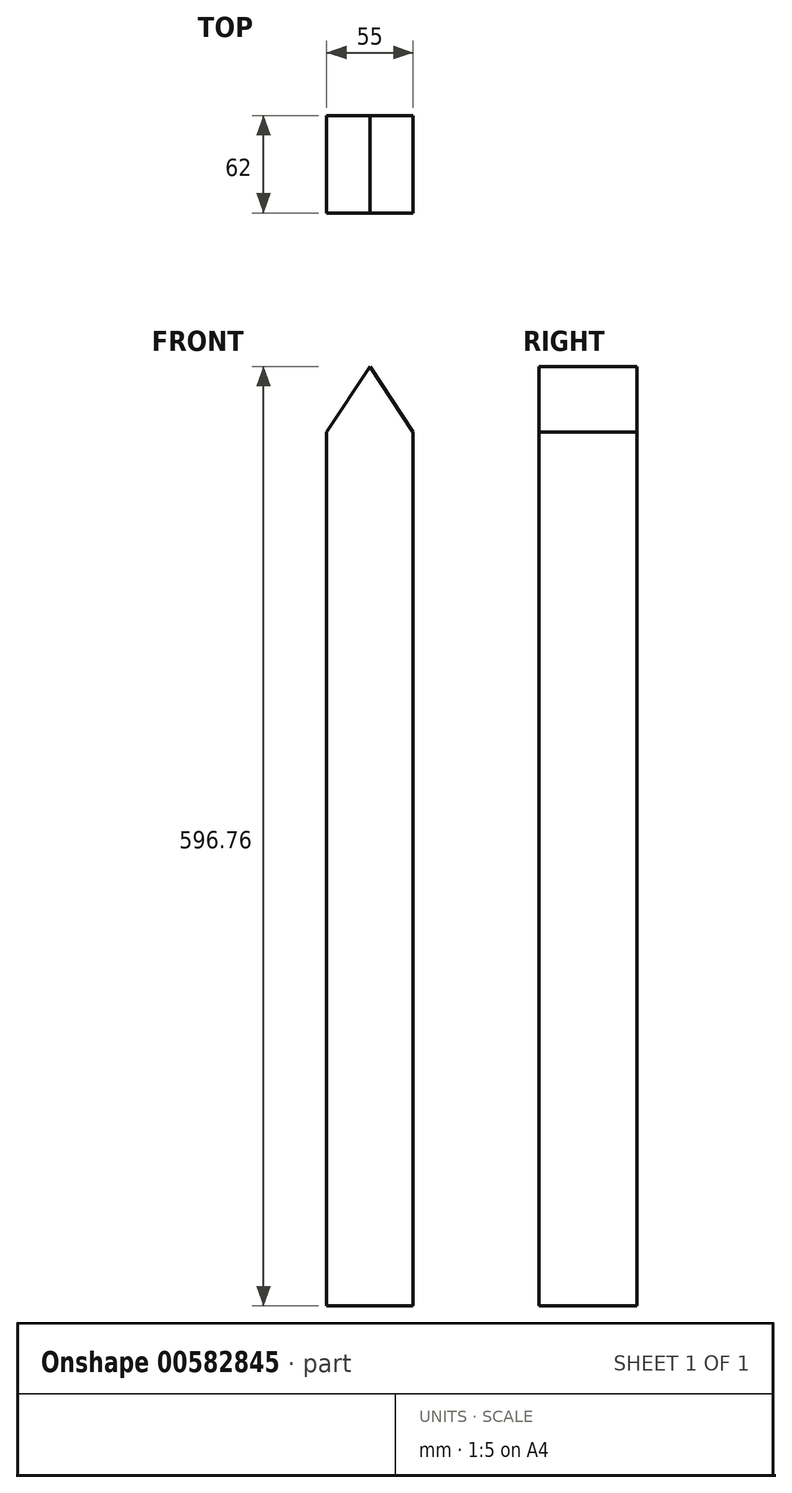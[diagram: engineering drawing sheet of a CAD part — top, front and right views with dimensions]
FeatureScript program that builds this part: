
annotation { "Feature Type Name" : "Feature", "Feature Type Description" : "" }
export const myFeature = defineFeature(function(context is Context, id is Id, definition is map)
    precondition{}
    {
        {
            var Q0;
            Q0=qCreatedBy(makeId("Front.planeOp"),FACE);
            var sketch = newSketch(context, id + "F0", { "sketchPlane" : qUnion([Q0])});
            skLineSegment(sketch, "E0.bottom", {"start": v(0, 0) * mm, "end": v(0, 0) * mm});
            skLineSegment(sketch, "E1", {"start": v(0, 0) * mm, "end": v(0, 555) * mm});
            skLineSegment(sketch, "E2", {"start": v(0, 0) * mm, "end": v(55, 0) * mm});
            skLineSegment(sketch, "E3", {"start": v(55, 0) * mm, "end": v(55, 555) * mm});
            skLineSegment(sketch, "E4", {"start": v(55, 555) * mm, "end": v(0, 555) * mm});
            skLineSegment(sketch, "E5", {"start": v(0, 555) * mm, "end": v(27.5, 596.76) * mm});
            skLineSegment(sketch, "E6", {"start": v(55, 555) * mm, "end": v(27.5, 596.76) * mm});
            skSolve(sketch);
        }
        {
            var Q0;
            Q0=makeQuery(id+"F0.imprint","IMPRINT",FACE,{"disambiguationData":[TD([[makeQuery(id+"F0.imprint","IMPRINT",EDGE,{"derivedFrom":sQuery(id+"F0.wireOp",EDGE,"E1")}),-1.0]])]});
            var Q1;
            Q1=makeQuery(id+"F0.imprint","IMPRINT",FACE,{"disambiguationData":[TD([[makeQuery(id+"F0.imprint","IMPRINT",EDGE,{"derivedFrom":sQuery(id+"F0.wireOp",EDGE,"E4")}),-1.0]])]});
            extrude(context, id + "F1", {"entities" : qUnion([Q0, Q1]), "depth" : 62 * mm, "offsetDistance" : 25 * mm});
        }
    });
